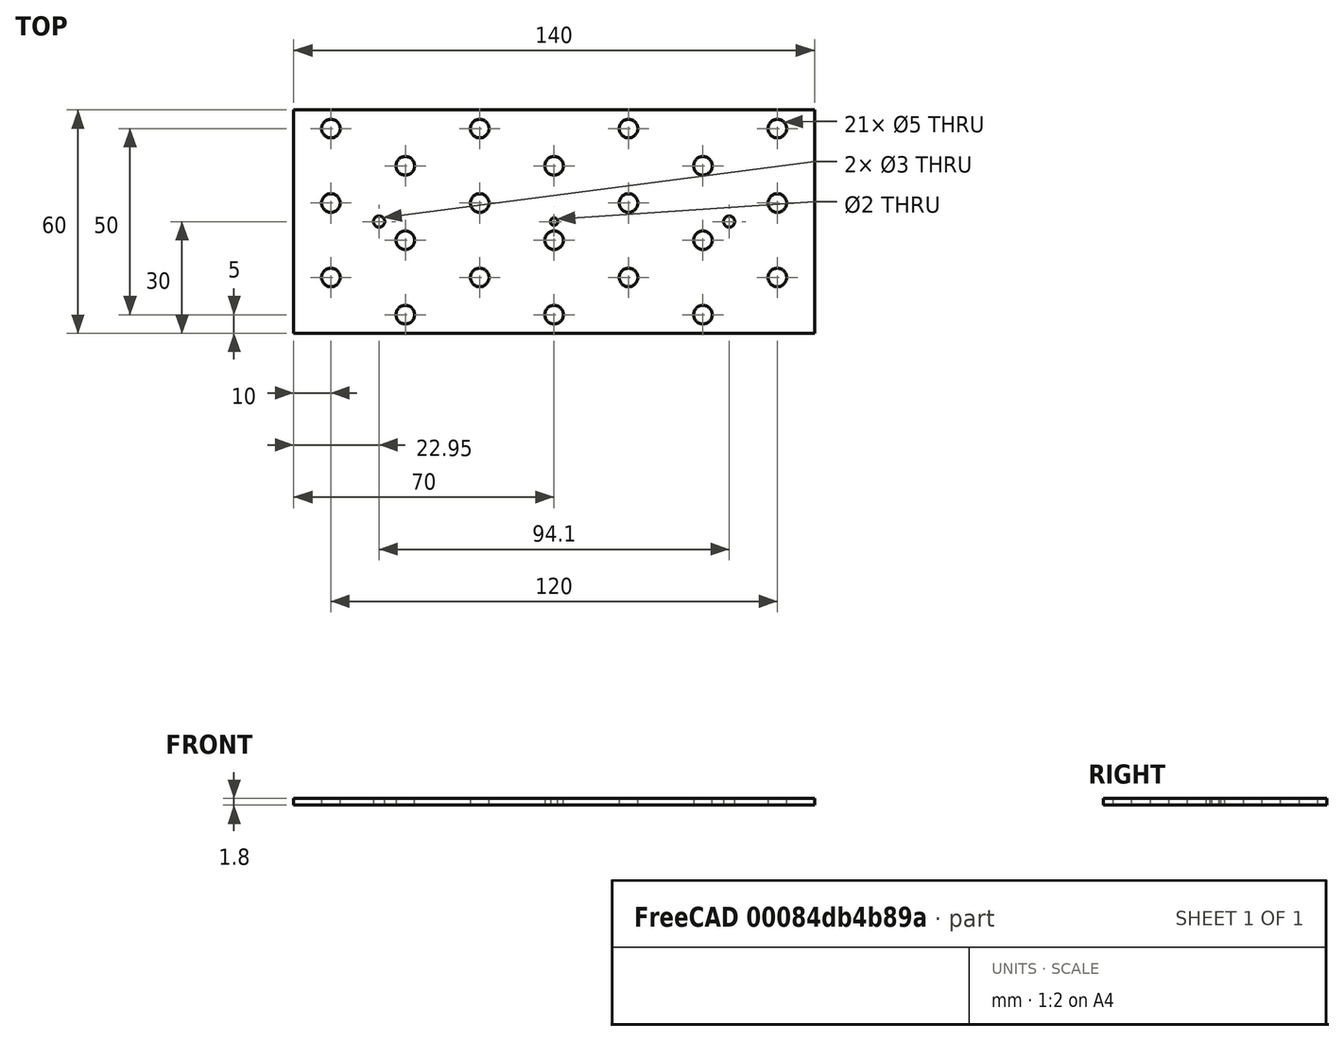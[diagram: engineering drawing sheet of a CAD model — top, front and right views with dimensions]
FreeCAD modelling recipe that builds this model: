
FCSTD DOCUMENT  (FreeCAD 0.19R24276 (Git))
Label: Bar_60x140__1_8mm
License: All rights reserved
LicenseURL: http://en.wikipedia.org/wiki/All_rights_reserved
objects: Sketcher::SketchObject×1, PartDesign::Pad×1, PartDesign::Body×1
note: 4 computed .brp shape members not serialized (recipe doc carries the construction recipe); baked Part::Feature solids carry a one-line shape summary decoded from their .brp

FEATURE [Sketcher::SketchObject] Sketch
  FullyConstrained = false
  MapMode = 5
  Support = -> [XY_Plane]
  sketch-geometry (51):
    g0: LineSegment StartX=0 StartY=0 StartZ=0 EndX=120 EndY=0 EndZ=0
    g1: LineSegment StartX=120 StartY=0 StartZ=0 EndX=120 EndY=80 EndZ=0
    g2: LineSegment StartX=120 StartY=80 StartZ=0 EndX=0 EndY=80 EndZ=0
    g3: LineSegment StartX=0 StartY=80 StartZ=0 EndX=0 EndY=0 EndZ=0
    g4: LineSegment StartX=0 StartY=4.5 StartZ=0 EndX=120 EndY=4.5 EndZ=0
    g5: LineSegment StartX=0 StartY=24.5 StartZ=0 EndX=120 EndY=24.5 EndZ=0
    g6: LineSegment StartX=0 StartY=44.5 StartZ=0 EndX=120 EndY=44.5 EndZ=0
    g7: LineSegment StartX=0 StartY=64.5 StartZ=0 EndX=120 EndY=64.5 EndZ=0
    g8: LineSegment StartX=48.5 StartY=0 StartZ=0 EndX=48.5 EndY=4.5 EndZ=0
    g9: LineSegment StartX=68.5 StartY=0 StartZ=0 EndX=68.5 EndY=4.5 EndZ=0
    g10: LineSegment StartX=88.5 StartY=0 StartZ=0 EndX=88.5 EndY=4.5 EndZ=0
    g11: LineSegment StartX=108.5 StartY=0 StartZ=0 EndX=108.5 EndY=4.5 EndZ=0
    g12: LineSegment StartX=0 StartY=14.5 StartZ=0 EndX=120 EndY=14.5 EndZ=0
    g13: LineSegment StartX=0 StartY=34.5 StartZ=0 EndX=120 EndY=34.5 EndZ=0
    g14: LineSegment StartX=0 StartY=54.5 StartZ=0 EndX=120 EndY=54.5 EndZ=0
    g15: LineSegment StartX=0 StartY=74.5 StartZ=0 EndX=120 EndY=74.5 EndZ=0
    g16: LineSegment StartX=48.5 StartY=24.5 StartZ=0 EndX=48.5 EndY=80 EndZ=0
    g17: LineSegment StartX=68.5 StartY=14.5 StartZ=0 EndX=68.5 EndY=80 EndZ=0
    g18: LineSegment StartX=88.5 StartY=24.5 StartZ=0 EndX=88.5 EndY=80 EndZ=0
    g19: LineSegment StartX=108.5 StartY=14.5 StartZ=0 EndX=108.5 EndY=80 EndZ=0
    g20: Circle CenterX=28.5 CenterY=14.5 CenterZ=0 NormalX=0 NormalY=0 NormalZ=1 AngleXU=0 Radius=2.5
    g21: Circle CenterX=108.5 CenterY=14.5 CenterZ=0 NormalX=0 NormalY=0 NormalZ=1 AngleXU=0 Radius=2.5
    g22: Circle CenterX=8.5 CenterY=24.5 CenterZ=0 NormalX=0 NormalY=0 NormalZ=1 AngleXU=0 Radius=2.5
    g23: Circle CenterX=48.5 CenterY=24.5 CenterZ=0 NormalX=0 NormalY=0 NormalZ=1 AngleXU=0 Radius=2.5
    g24: Circle CenterX=88.5 CenterY=24.5 CenterZ=0 NormalX=0 NormalY=0 NormalZ=1 AngleXU=0 Radius=2.5
    g25: Circle CenterX=8.5 CenterY=44.5 CenterZ=0 NormalX=0 NormalY=0 NormalZ=1 AngleXU=0 Radius=2.5
    g26: Circle CenterX=48.5 CenterY=44.5 CenterZ=0 NormalX=0 NormalY=0 NormalZ=1 AngleXU=0 Radius=2.5
    g27: Circle CenterX=88.5 CenterY=44.5 CenterZ=0 NormalX=0 NormalY=0 NormalZ=1 AngleXU=0 Radius=2.5
    g28: Circle CenterX=28.5 CenterY=54.5 CenterZ=0 NormalX=0 NormalY=0 NormalZ=1 AngleXU=0 Radius=2.5
    g29: Circle CenterX=68.5 CenterY=54.5 CenterZ=0 NormalX=0 NormalY=0 NormalZ=1 AngleXU=0 Radius=2.5
    g30: Circle CenterX=108.5 CenterY=54.5 CenterZ=0 NormalX=0 NormalY=0 NormalZ=1 AngleXU=0 Radius=2.5
    g31: Circle CenterX=88.5 CenterY=64.5 CenterZ=0 NormalX=0 NormalY=0 NormalZ=1 AngleXU=0 Radius=2.5
    g32: Circle CenterX=48.5 CenterY=64.5 CenterZ=0 NormalX=0 NormalY=0 NormalZ=1 AngleXU=0 Radius=2.5
    g33: Circle CenterX=8.5 CenterY=64.5 CenterZ=0 NormalX=0 NormalY=0 NormalZ=1 AngleXU=0 Radius=2.5
    g34: Circle CenterX=28.5 CenterY=34.5 CenterZ=0 NormalX=0 NormalY=0 NormalZ=1 AngleXU=0 Radius=2.5
    g35: Circle CenterX=68.5 CenterY=34.5 CenterZ=0 NormalX=0 NormalY=0 NormalZ=1 AngleXU=0 Radius=2.5
    g36: Circle CenterX=108.5 CenterY=34.5 CenterZ=0 NormalX=0 NormalY=0 NormalZ=1 AngleXU=0 Radius=2.5
    g37: LineSegment StartX=28.5 StartY=74.5 StartZ=0 EndX=28.5 EndY=14.5 EndZ=0
    g38: LineSegment StartX=8.5 StartY=4.5 StartZ=0 EndX=8.5 EndY=24.5 EndZ=0
    g39: Circle CenterX=68.5 CenterY=14.5 CenterZ=0 NormalX=0 NormalY=0 NormalZ=1 AngleXU=0 Radius=2.5
    g40: LineSegment StartX=-1.5 StartY=9.5 StartZ=0 EndX=138.5 EndY=9.5 EndZ=0
    g41: LineSegment StartX=-1.5 StartY=69.5 StartZ=0 EndX=138.5 EndY=69.5 EndZ=0
    g42: LineSegment StartX=-1.5 StartY=69.5 StartZ=0 EndX=-1.5 EndY=9.5 EndZ=0
    g43: LineSegment StartX=138.5 StartY=69.5 StartZ=0 EndX=138.5 EndY=9.5 EndZ=0
    g44: Circle CenterX=128.5 CenterY=24.5 CenterZ=0 NormalX=0 NormalY=0 NormalZ=1 AngleXU=0 Radius=2.5
    g45: Circle CenterX=128.5 CenterY=44.5 CenterZ=0 NormalX=0 NormalY=0 NormalZ=1 AngleXU=0 Radius=2.5
    g46: Circle CenterX=128.5 CenterY=64.5 CenterZ=0 NormalX=0 NormalY=0 NormalZ=1 AngleXU=0 Radius=2.5
    g47: Circle CenterX=68.5 CenterY=39.5 CenterZ=0 NormalX=0 NormalY=0 NormalZ=1 AngleXU=0 Radius=1
    g48: LineSegment StartX=68.5 StartY=39.5 StartZ=0 EndX=138.5 EndY=39.5 EndZ=0
    g49: Circle CenterX=115.55 CenterY=39.5 CenterZ=0 NormalX=0 NormalY=0 NormalZ=1 AngleXU=0 Radius=1.5
    g50: Circle CenterX=21.4498 CenterY=39.5 CenterZ=0 NormalX=0 NormalY=0 NormalZ=1 AngleXU=0 Radius=1.5
  constraints (108):
    c: Coincident(g0,g1)
    c: Coincident(g1,g2)
    c: Coincident(g2,g3)
    c: Coincident(g3,g0)
    c: Horizontal(g0)
    c: Horizontal(g2)
    c: Vertical(g1)
    c: Vertical(g3)
    c: Coincident(g0,g-1)
    c: DistanceX(g0,g0) = 120
    c: DistanceY(g3,g3) = 80
    c: Horizontal(g4)
    c: PointOnObject(g4,g3)
    c: PointOnObject(g4,g1)
    c: Horizontal(g5)
    c: PointOnObject(g5,g3)
    c: PointOnObject(g5,g1)
    c: DistanceY(g4,g5) = 20
    c: Horizontal(g6)
    c: PointOnObject(g6,g1)
    c: PointOnObject(g6,g3)
    c: DistanceY(g5,g6) = 20
    c: Horizontal(g7)
    c: PointOnObject(g7,g1)
    c: PointOnObject(g7,g3)
    c: DistanceY(g6,g7) = 20
    c: Vertical(g8)
    c: Vertical(g9)
    c: Vertical(g10)
    c: Vertical(g11)
    c: PointOnObject(g8,g0)
    c: PointOnObject(g9,g0)
    c: PointOnObject(g10,g0)
    c: PointOnObject(g11,g0)
    c: PointOnObject(g19,g2)
    c: PointOnObject(g18,g2)
    c: PointOnObject(g17,g2)
    c: PointOnObject(g16,g2)
    c: DistanceX(g8,g9) = 20
    c: DistanceX(g9,g10) = 20
    c: DistanceX(g10,g11) = 20
    c: Horizontal(g12)
    c: Horizontal(g13)
    c: Horizontal(g14)
    c: Horizontal(g15)
    c: PointOnObject(g12,g3)
    c: PointOnObject(g13,g3)
    c: PointOnObject(g14,g3)
    c: PointOnObject(g15,g3)
    c: PointOnObject(g15,g1)
    c: PointOnObject(g14,g1)
    c: PointOnObject(g13,g1)
    c: PointOnObject(g12,g1)
    c: DistanceY(g0,g12) = 14.5
    c: DistanceY(g12,g13) = 20
    c: DistanceY(g13,g14) = 20
    c: DistanceY(g14,g15) = 20
    c: PointOnObject(g20,g12)
    c: PointOnObject(g8,g4)
    c: Tangent(g8,g16)
    c: PointOnObject(g9,g4)
    c: PointOnObject(g17,g12)
    c: Tangent(g9,g17)
    c: PointOnObject(g10,g4)
    c: Tangent(g10,g18)
    c: PointOnObject(g11,g4)
    c: PointOnObject(g19,g12)
    c: Tangent(g11,g19)
    c: Coincident(g21,g19)
    c: Diameter(g20) = 5
    c: PointOnObject(g16,g5)
    c: PointOnObject(g18,g5)
    c: Equal(g23,g24)
    c: Equal(g33,g28)
    c: Equal(g28,g32)
    c: Equal(g32,g31)
    c: Equal(g31,g30)
    c: Diameter(g28) = 5
    c: Equal(g31,g29)
    c: Equal(g26,g27)
    c: Diameter(g34) = 5
    c: Coincident(g37,g20)
    c: Vertical(g37)
    c: DistanceY(g0,g4) = 4.5
    c: Coincident(g38,g22)
    c: Vertical(g38)
    c: Coincident(g39,g17)
    c: Equal(g21,g39)
    c: Horizontal(g40)
    c: Horizontal(g41)
    c: Vertical(g42)
    c: DistanceX(g0,g38) = 8.5
    c: Coincident(g42,g40)
    c: Coincident(g41,g42)
    c: Vertical(g43)
    c: DistanceX(g40,g38) = 10
    c: Coincident(g40,g43)
    c: DistanceY(g40,g21) = 5
    c: Coincident(g41,g43)
    c: DistanceY(g40,g41) = 60
    c: DistanceX(g41,g41) = 140
    c: Diameter(g47) = 2
    c: Coincident(g48,g47)
    c: Horizontal(g48)
    c: PointOnObject(g48,g43)
    c: PointOnObject(g49,g48)
    c: Diameter(g49) = 3
    c: Diameter(g50) = 3
FEATURE [PartDesign::Pad] Pad
  Direction = (1,1,1)
  Length = 1.8
  Length2 = 100
  Profile = -> Sketch
  Type = 0
FEATURE [PartDesign::Body] Body
  Group = -> [Sketch,Pad]
  Origin = -> Origin
  Tip = -> Pad
